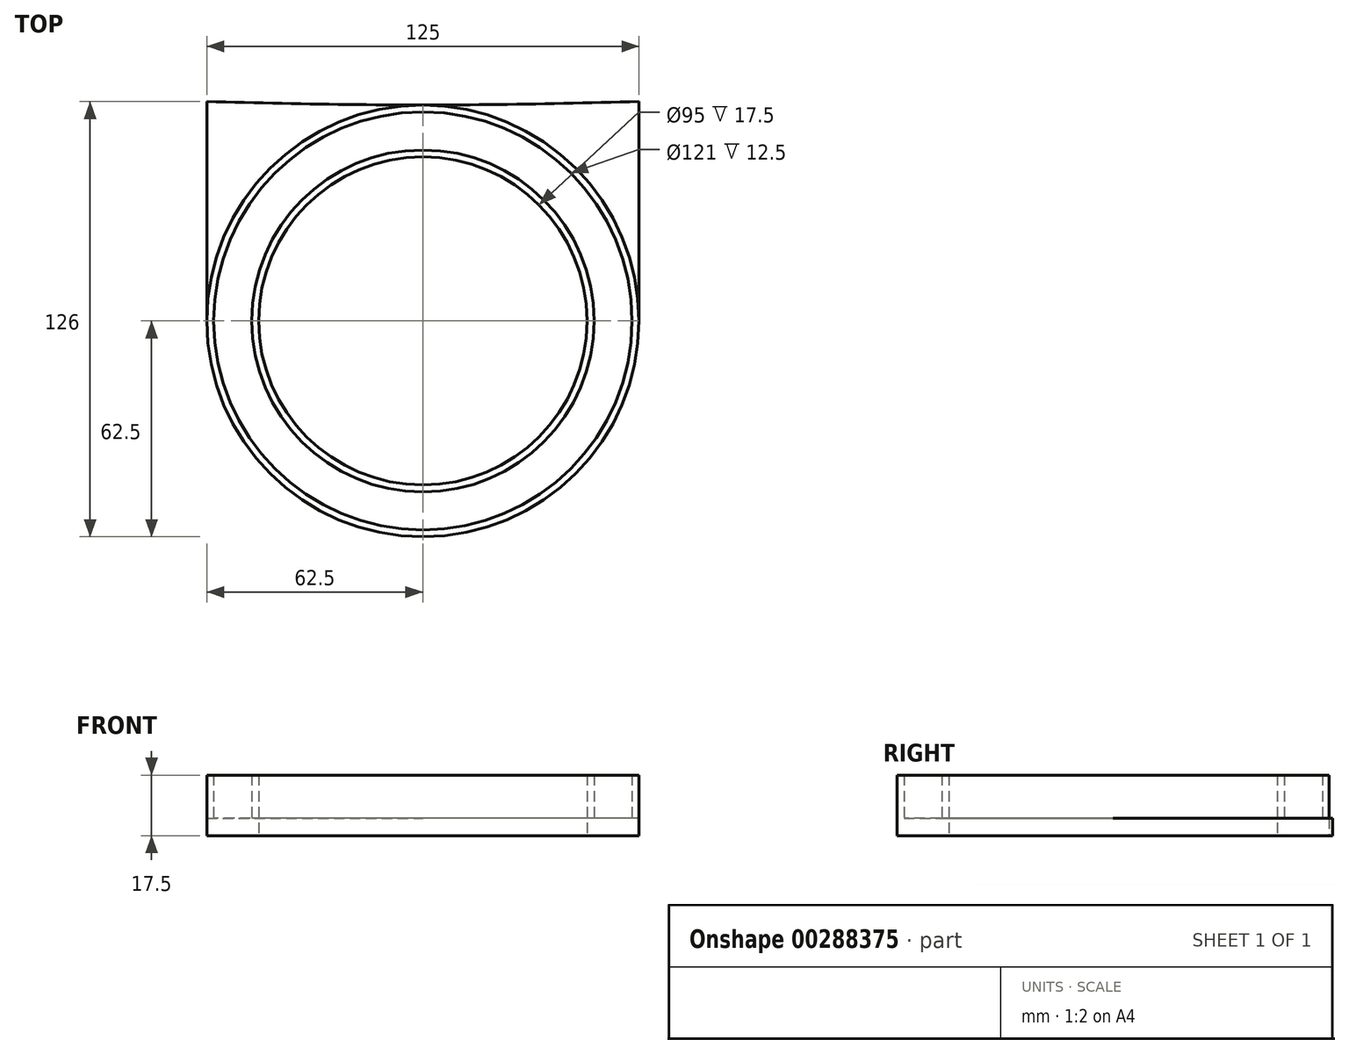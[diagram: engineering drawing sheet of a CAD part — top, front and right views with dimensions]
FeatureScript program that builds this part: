
annotation { "Feature Type Name" : "Feature", "Feature Type Description" : "" }
export const myFeature = defineFeature(function(context is Context, id is Id, definition is map)
    precondition{}
    {
        {
            var Q0;
            Q0=qCreatedBy(makeId("Top.planeOp"),FACE);
            var sketch = newSketch(context, id + "F0", { "sketchPlane" : qUnion([Q0])});
            skCircle(sketch, "E0", {"center": v(0, 0) * mm, "radius": 62.5 * mm});
            skLineSegment(sketch, "E1", {"start": v(-62.5, 0) * mm, "end": v(-62.5, 63.5) * mm});
            skLineSegment(sketch, "E2", {"start": v(62.5, 63.5) * mm, "end": v(62.5, 0) * mm});
            skCircle(sketch, "E3", {"center": v(0, 0) * mm, "radius": 47.5 * mm});
            skPoint(sketch, "E4.1.internal.snap0", {"position": v(0, 63.5) * mm});
            skFitSpline(sketch, "E4", {"points": [v(-62.5, 63.5) * mm, v(0, 62.5) * mm, v(62.5, 63.5) * mm], "startDerivative": vector(125, -3) * mm, "endDerivative": vector(125, 3) * mm});
            skSolve(sketch);
        }
        {
            var Q0;
            Q0 = qSketchRegion(id + "F0", true);
            extrude(context, id + "F1", {"entities" : qUnion([Q0]), "depth" : 5 * mm, "offsetDistance" : 25 * mm});
        }
        {
            var Q0;
            Q0=makeQuery(id+"F1.opExtrude","CAP_FACE",FACE,{"disambiguationData":[OSD([sQuery(id+"F0.wireOp",EDGE,"E0"),sQuery(id+"F0.wireOp",EDGE,"E1"),sQuery(id+"F0.wireOp",EDGE,"xpD0ogJE-QtS8-HGP8-6Zjr-eTTQFVP8pLG3"),sQuery(id+"F0.wireOp",EDGE,"E2")])],"isStart":false});
            var sketch = newSketch(context, id + "F2", { "sketchPlane" : qUnion([Q0])});
            skCircle(sketch, "E5", {"center": v(0, 0) * mm, "radius": 62.5 * mm});
            skCircle(sketch, "E6", {"center": v(0, 0) * mm, "radius": 47.5 * mm});
            skCircle(sketch, "E7", {"center": v(0, 0) * mm, "radius": 60.5 * mm});
            skCircle(sketch, "E8", {"center": v(0, 0) * mm, "radius": 49.5 * mm});
            skSolve(sketch);
        }
        {
            var Q0;
            Q0 = qSketchRegion(id + "F2", true);
            var Q1;
            Q1=makeQuery(id+"F2.imprint","IMPRINT",FACE,{"disambiguationData":[TD([[makeQuery(id+"F2.imprint","IMPRINT",EDGE,{"derivedFrom":sQuery(id+"F2.wireOp",EDGE,"E6")}),-1.0]])]});
            extrude(context, id + "F3", {"entities" : qUnion([Q0, Q1]), "operationType" : NewBodyOperationType.ADD, "depth" : 12.5 * mm, "offsetDistance" : 25 * mm});
        }
    });
